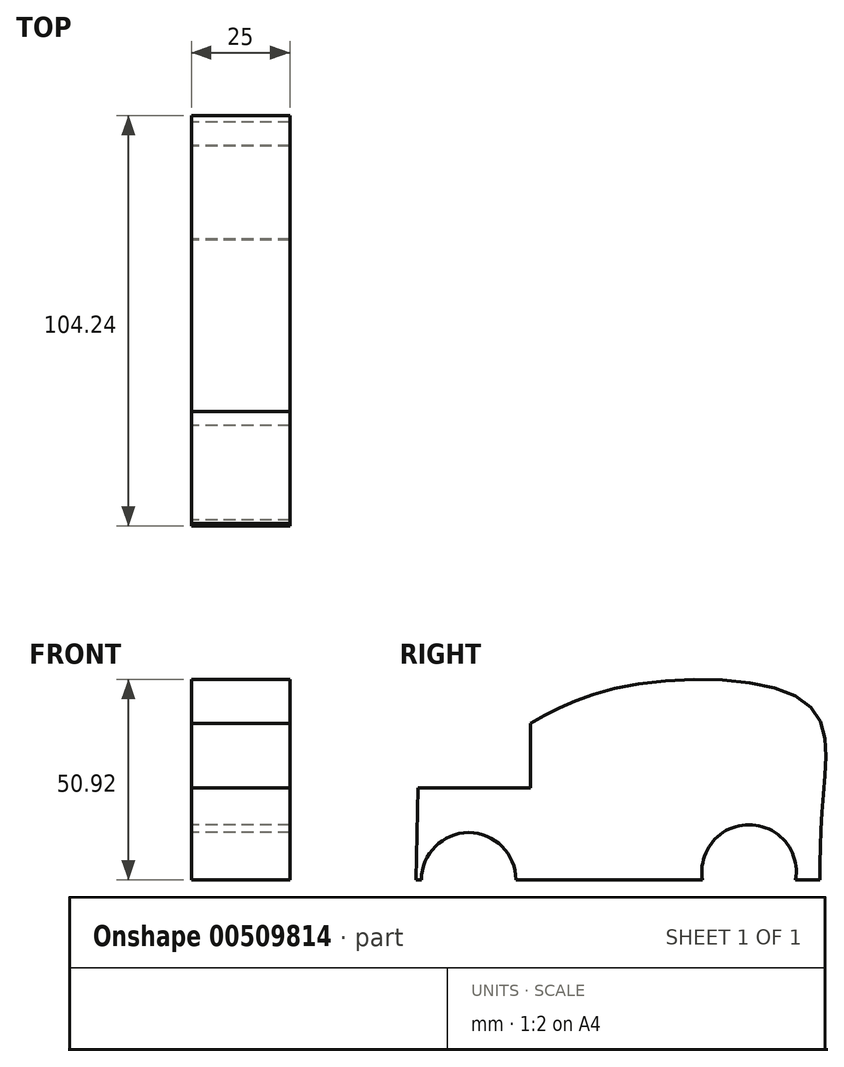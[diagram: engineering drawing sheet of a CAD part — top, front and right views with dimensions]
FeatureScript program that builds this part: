
annotation { "Feature Type Name" : "Feature", "Feature Type Description" : "" }
export const myFeature = defineFeature(function(context is Context, id is Id, definition is map)
    precondition{}
    {
        {
            var Q0;
            Q0=qCreatedBy(makeId("Right.planeOp"),FACE);
            var sketch = newSketch(context, id + "F0", { "sketchPlane" : qUnion([Q0])});
            skLineSegment(sketch, "E0", {"start": v(-53.12, 0) * mm, "end": v(49.52, 0) * mm});
            skLineSegment(sketch, "E1", {"start": v(-23.99, 39.79) * mm, "end": v(-23.99, 23.42) * mm});
            skLineSegment(sketch, "E2", {"start": v(-23.99, 23.42) * mm, "end": v(-52.54, 23.42) * mm});
            skLineSegment(sketch, "E3", {"start": v(-53.12, 0) * mm, "end": v(-52.54, 23.42) * mm});
            skCircle(sketch, "E4", {"center": v(-39.66, 0) * mm, "radius": 12 * mm});
            skCircle(sketch, "E5", {"center": v(31.56, 2) * mm, "radius": 12 * mm});
            skFitSpline(sketch, "E6", {"points": [v(-23.99, 39.79) * mm, v(0, 49.15) * mm, v(46.69, 44.42) * mm, v(50.44, 21.9) * mm, v(49.52, 0) * mm], "startDerivative": vector(81.68, 45.85) * mm, "endDerivative": vector(-1.32, -95.72) * mm});
            skSolve(sketch);
        }
        {
            var Q0;
            Q0=makeQuery(id+"F0.imprint","IMPRINT",FACE,{"disambiguationData":[TD([[makeQuery(id+"F0.imprint","IMPRINT",EDGE,{"derivedFrom":sQuery(id+"F0.wireOp",EDGE,"E1")}),1.0]])]});
            extrude(context, id + "F1", {"entities" : qUnion([Q0]), "depth" : 25 * mm, "offsetDistance" : 25 * mm});
        }
    });
